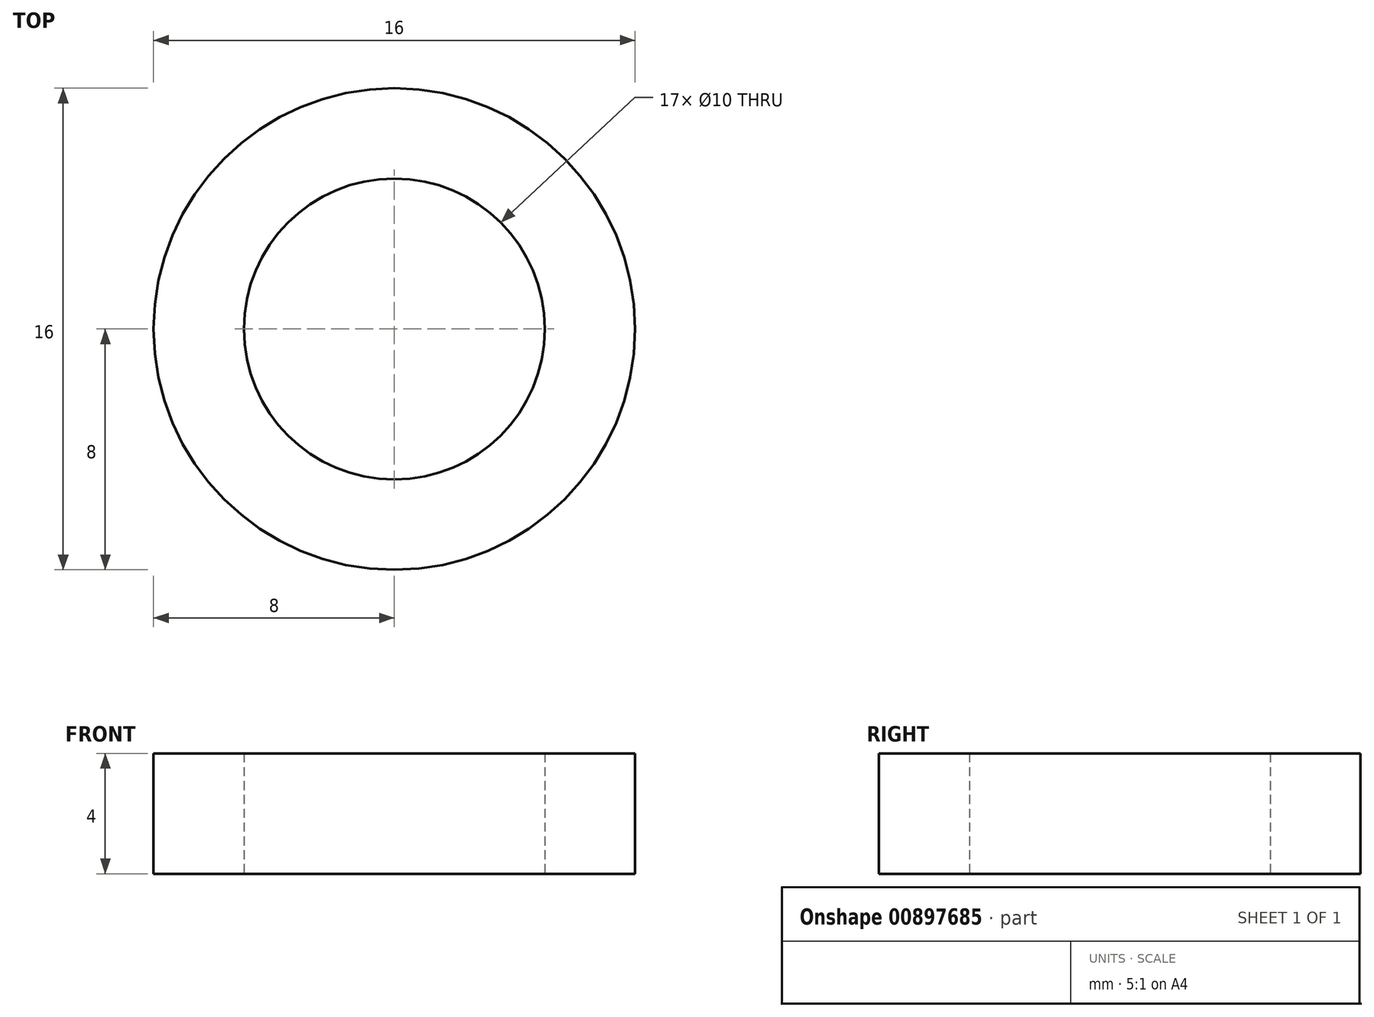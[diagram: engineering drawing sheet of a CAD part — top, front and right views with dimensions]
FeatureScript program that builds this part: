
annotation { "Feature Type Name" : "Feature", "Feature Type Description" : "" }
export const myFeature = defineFeature(function(context is Context, id is Id, definition is map)
    precondition{}
    {
        {
            var Q0;
            Q0=qCreatedBy(makeId("Top.planeOp"),FACE);
            var sketch = newSketch(context, id + "F0", { "sketchPlane" : qUnion([Q0])});
            skCircle(sketch, "E0", {"center": v(0, 0) * mm, "radius": 5 * mm});
            skCircle(sketch, "E1", {"center": v(0, 0) * mm, "radius": 8 * mm});
            skSolve(sketch);
        }
        {
            var Q0;
            Q0 = qSketchRegion(id + "F0", true);
            extrude(context, id + "F1", {"entities" : qUnion([Q0]), "depth" : 4 * mm, "offsetDistance" : 25 * mm});
        }
    });
